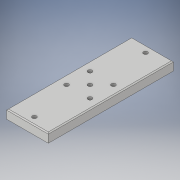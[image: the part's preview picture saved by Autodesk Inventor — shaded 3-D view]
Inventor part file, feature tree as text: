
AUTODESK INVENTOR PART (.ipt)
format: ipt  version: 2019.4 (Build 234330000, 330)  size: 150,016 bytes
history: native  units: in
note: dims shown in document units (in); Inventor stores cm internally (conversion verified against a paired STEP export)
features: sketch x5, extrude x4, hole x1, fillet x1, chamfer x1
ambient origin geometry x8: Origin, YZ Plane, XZ Plane, XY Plane, X Axis, Y Axis, Z Axis, Center Point
bodies: Solid1 (feature_tree)
feature tree (12):
  extrude  "Extrusion1"  Depth=1.181in
  hole  "Hole1"  [1 undecoded]
  extrude  "Extrusion2"  Depth=0.7874in
  extrude  "Extrusion3"  Depth=0.059in
  fillet  "Fillet1"  Radius=0.25in
  extrude  "Extrusion4"  Depth=0.315in
  chamfer  "Chamfer2"  Distance=2.756in
  sketch  "Sketch1"  dims[d0=3.543in d1=1.181in]
  sketch  "Sketch2"  dims[d2=0.25in d3=0.0in d4=0.118in]
  sketch  "Sketch3"  dims[d5=0.3315in d6=0.7874in d8=0.663in d9=0.7874in d11=0.663in]
  sketch  "Sketch4"  dims[d14=0.3315in]
  sketch  "Sketch5"  dims[d15=0.118in d16=0.18in d17=0.375in d18=0.25in d19=0.5635in d20=0.22in d21=0.8108in d22=0.118in d23=0.25in d24=0.0in d25=0.315in d26=2.756in d27=0.059in d28=0.0in d29=0.08in d33=0.118in d34=0.118in d35=0.197in d36=0.197in d37=0.059in d38=0.0in d39=0.028in d40=0.125in d41=45.0deg]
note: 1 required parameter value undecoded (feature->parameter linkage not recoverable at this tier; creation-order binding heuristic only, values carry confidence <= 0.55)
